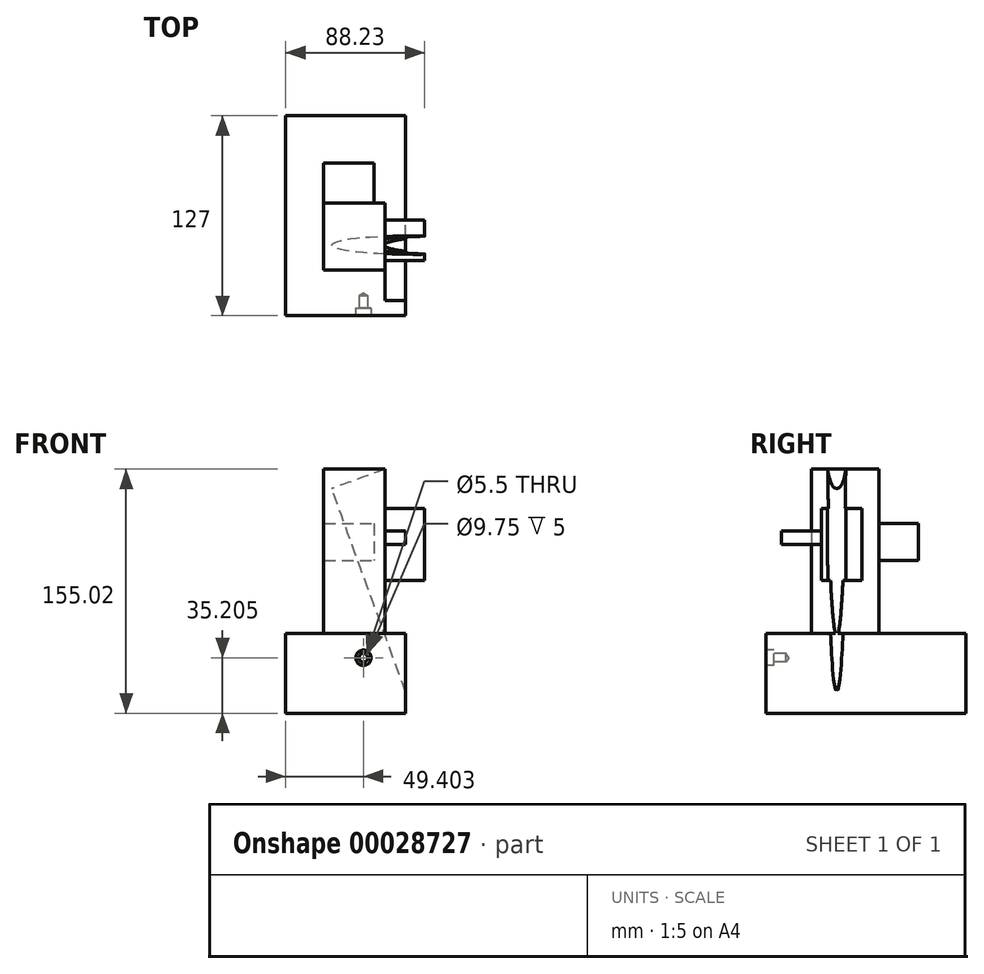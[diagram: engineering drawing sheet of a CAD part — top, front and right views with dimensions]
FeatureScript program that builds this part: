
annotation { "Feature Type Name" : "Feature", "Feature Type Description" : "" }
export const myFeature = defineFeature(function(context is Context, id is Id, definition is map)
    precondition{}
    {
        {
            var Q0;
            Q0=qCreatedBy(makeId("Front.planeOp"),FACE);
            var sketch = newSketch(context, id + "F0", { "sketchPlane" : qUnion([Q0])});
            skLineSegment(sketch, "E0.bottom", {"start": v(-76.2, 50.8) * mm, "end": v(0, 50.8) * mm});
            skLineSegment(sketch, "E0.top", {"start": v(-76.2, 0) * mm, "end": v(0, 0) * mm});
            skLineSegment(sketch, "E0.left", {"start": v(-76.2, 50.8) * mm, "end": v(-76.2, 0) * mm});
            skLineSegment(sketch, "E0.right", {"start": v(0, 50.8) * mm, "end": v(0, 0) * mm});
            skSolve(sketch);
        }
        {
            var Q0;
            Q0=makeQuery(id+"F0.imprint","IMPRINT",FACE,{"disambiguationData":[TD([[makeQuery(id+"F0.imprint","IMPRINT",EDGE,{"derivedFrom":sQuery(id+"F0.wireOp",EDGE,"E0.bottom")}),-1.0]])]});
            extrude(context, id + "F1", {"entities" : qUnion([Q0]), "depth" : 127 * mm});
        }
        {
            var Q0;
            Q0=makeQuery(id+"F1.opExtrude","SWEPT_FACE",FACE,{"disambiguationData":[OSD([sQuery(id+"F0.wireOp",EDGE,"E0.bottom")])]});
            var sketch = newSketch(context, id + "F2", { "sketchPlane" : qUnion([Q0])});
            skLineSegment(sketch, "E1.bottom", {"start": v(-12.97, -55.55) * mm, "end": v(-52.05, -55.55) * mm});
            skLineSegment(sketch, "E1.top", {"start": v(-12.97, -98.12) * mm, "end": v(-52.05, -98.12) * mm});
            skLineSegment(sketch, "E1.left", {"start": v(-12.97, -55.55) * mm, "end": v(-12.97, -98.12) * mm});
            skLineSegment(sketch, "E1.right", {"start": v(-52.05, -55.55) * mm, "end": v(-52.05, -98.12) * mm});
            skSolve(sketch);
        }
        {
            var Q0;
            Q0=makeQuery(id+"F2.imprint","IMPRINT",FACE,{"disambiguationData":[TD([[makeQuery(id+"F2.imprint","IMPRINT",EDGE,{"derivedFrom":sQuery(id+"F2.wireOp",EDGE,"E1.bottom")}),1.0]])]});
            extrude(context, id + "F3", {"entities" : qUnion([Q0]), "operationType" : NewBodyOperationType.ADD, "offsetDistance" : 25.4 * mm, "depth" : 104.22 * mm});
        }
        {
            var Q0;
            Q0=makeQuery(id+"F3.opExtrude","SWEPT_FACE",FACE,{"disambiguationData":[OSD([sQuery(id+"F2.wireOp",EDGE,"E1.left")])]});
            var sketch = newSketch(context, id + "F4", { "sketchPlane" : qUnion([Q0])});
            skLineSegment(sketch, "E2.bottom", {"start": v(-66.31, 129.97) * mm, "end": v(-91.94, 129.97) * mm});
            skLineSegment(sketch, "E2.top", {"start": v(-66.31, 84.44) * mm, "end": v(-91.94, 84.44) * mm});
            skLineSegment(sketch, "E2.left", {"start": v(-66.31, 129.97) * mm, "end": v(-66.31, 84.44) * mm});
            skLineSegment(sketch, "E2.right", {"start": v(-91.94, 129.97) * mm, "end": v(-91.94, 84.44) * mm});
            skSolve(sketch);
        }
        {
            var Q0;
            Q0=makeQuery(id+"F4.imprint","IMPRINT",FACE,{"disambiguationData":[TD([[makeQuery(id+"F4.imprint","IMPRINT",EDGE,{"derivedFrom":sQuery(id+"F4.wireOp",EDGE,"E2.bottom")}),1.0]])]});
            extrude(context, id + "F5", {"entities" : qUnion([Q0]), "operationType" : NewBodyOperationType.ADD, "depth" : 25 * mm, "offsetDistance" : 25.4 * mm});
        }
        {
            var Q0;
            Q0=makeQuery(id+"F5.opExtrude","SWEPT_FACE",FACE,{"disambiguationData":[OSD([sQuery(id+"F4.wireOp",EDGE,"E2.right")])]});
            var sketch = newSketch(context, id + "F6", { "sketchPlane" : qUnion([Q0])});
            skLineSegment(sketch, "E3.bottom", {"start": v(0, 115.63) * mm, "end": v(-12.97, 115.63) * mm});
            skLineSegment(sketch, "E3.top", {"start": v(0, 107.2) * mm, "end": v(-12.97, 107.2) * mm});
            skLineSegment(sketch, "E3.left", {"start": v(0, 115.63) * mm, "end": v(0, 107.2) * mm});
            skLineSegment(sketch, "E3.right", {"start": v(-12.97, 115.63) * mm, "end": v(-12.97, 107.2) * mm});
            skSolve(sketch);
        }
        {
            var Q0;
            Q0 = qSketchRegion(id + "F6", true);
            extrude(context, id + "F7", {"entities" : qUnion([Q0]), "operationType" : NewBodyOperationType.ADD, "depth" : 25.4 * mm, "offsetDistance" : 25.4 * mm});
        }
        {
            var Q0;
            Q0=makeQuery(id+"F5.opExtrude","CAP_FACE",FACE,{"disambiguationData":[OSD([sQuery(id+"F4.wireOp",EDGE,"E2.bottom"),sQuery(id+"F4.wireOp",EDGE,"E2.top"),sQuery(id+"F4.wireOp",EDGE,"E2.left"),sQuery(id+"F4.wireOp",EDGE,"E2.right")])],"isStart":false});
            var sketch = newSketch(context, id + "F8", { "sketchPlane" : qUnion([Q0])});
            skCircle(sketch, "E4", {"center": v(-78.65, 114.91) * mm, "radius": 9.43 * mm});
            skSolve(sketch);
        }
        {
            var Q0;
            Q0=sQuery(id+"F8.wireOp",EDGE,"E4");
            extrude(context, id + "F9", {"bodyType" : ToolBodyType.SURFACE, "surfaceEntities" : qUnion([Q0]), "depth" : 25.4 * mm, "offsetDistance" : 25.4 * mm});
        }
        {
            var Q0;
            Q0=makeQuery(id+"F3.opExtrude","SWEPT_FACE",FACE,{"disambiguationData":[OSD([sQuery(id+"F2.wireOp",EDGE,"E1.bottom")])]});
            var sketch = newSketch(context, id + "F10", { "sketchPlane" : qUnion([Q0])});
            skLineSegment(sketch, "E5.bottom", {"start": v(52.05, 120.5) * mm, "end": v(20.21, 120.5) * mm});
            skLineSegment(sketch, "E5.top", {"start": v(52.05, 96.9) * mm, "end": v(20.21, 96.9) * mm});
            skLineSegment(sketch, "E5.left", {"start": v(52.05, 120.5) * mm, "end": v(52.05, 96.9) * mm});
            skLineSegment(sketch, "E5.right", {"start": v(20.21, 120.5) * mm, "end": v(20.21, 96.9) * mm});
            skSolve(sketch);
        }
        {
            var Q0;
            Q0=makeQuery(id+"F10.imprint","IMPRINT",FACE,{"disambiguationData":[TD([[makeQuery(id+"F10.imprint","IMPRINT",EDGE,{"derivedFrom":sQuery(id+"F10.wireOp",EDGE,"E5.bottom")}),1.0]])]});
            extrude(context, id + "F11", {"entities" : qUnion([Q0]), "operationType" : NewBodyOperationType.ADD, "depth" : 25.4 * mm, "offsetDistance" : 25.4 * mm});
        }
        {
            var Q0;
            Q0=makeQuery(id+"F3.opExtrude","CAP_EDGE",EDGE,{"disambiguationData":[OSD([sQuery(id+"F2.wireOp",EDGE,"E1.left")])],"isStart":false});
            cPlane(context, id + "F12", {"entities" : qUnion([Q0]), "cplaneType" : CPlaneType.LINE_ANGLE, "offset" : 25.4 * mm, "angle" : 20 * degree, "width" : 152.4 * mm, "height" : 152.4 * mm});
        }
        {
            var Q0;
            Q0=qCreatedBy(id+"F12.planeOp",FACE);
            var sketch = newSketch(context, id + "F13", { "sketchPlane" : qUnion([Q0])});
            skEllipse(sketch, "E6", {"center": v(51.65, 82.17) * mm, "majorRadius": 47 * mm, "minorRadius": 5.86 * mm, "majorAxis": v(-1, 0)});
            skSolve(sketch);
        }
        {
            var Q0;
            Q0 = qSketchRegion(id + "F13", true);
            extrude(context, id + "F14", {"entities" : qUnion([Q0]), "operationType" : NewBodyOperationType.REMOVE, "depth" : 200 * mm, "offsetDistance" : 25.4 * mm});
        }
        {
            var Q0;
            Q0=makeQuery(id+"F1.opExtrude","CAP_FACE",FACE,{"disambiguationData":[OSD([sQuery(id+"F0.wireOp",EDGE,"E0.bottom"),sQuery(id+"F0.wireOp",EDGE,"E0.top"),sQuery(id+"F0.wireOp",EDGE,"E0.left"),sQuery(id+"F0.wireOp",EDGE,"E0.right")])],"isStart":false});
            var sketch = newSketch(context, id + "F15", { "sketchPlane" : qUnion([Q0])});
            skPoint(sketch, "E7", {"position": v(-26.8, 35.2) * mm});
            skSolve(sketch);
        }
        {
            var Q0;
            Q0=sQuery(id+"F15.wireOp",VERTEX,"E7");
            var Q1;
            Q1=makeQuery(id+"F1.opExtrude","SWEPT_BODY",BODY,{"disambiguationData":[OSD([sQuery(id+"F0.wireOp",EDGE,"E0.bottom"),sQuery(id+"F0.wireOp",EDGE,"E0.top"),sQuery(id+"F0.wireOp",EDGE,"E0.left"),sQuery(id+"F0.wireOp",EDGE,"E0.right")])]});
            hole(context, id + "F16", {"style" : HoleStyle.C_BORE, "endStyle" : HoleEndStyle.BLIND, "standardTappedOrClearance" : lookupTablePath({ "standard" : "ISO", "fit" : "Normal", "size" : "M5", "type" : "Clearance" }), "standardBlindInLast" : lookupTablePath({ "fit" : "Normal", "standard" : "ISO", "size" : "M5", "type" : "Clearance" }), "holeDiameter" : 5.5 * mm, "cBoreDiameter" : 9.75 * mm, "cBoreDepth" : 5 * mm, "majorDiameter" : 6.35 * mm, "holeDepth" : 12.7 * mm, "isTappedThrough" : true, "tappedDepth" : 12.7 * mm, "tapClearance" : 3, "locations" : qUnion([Q0]), "scope" : qUnion([Q1])});
        }
    });
